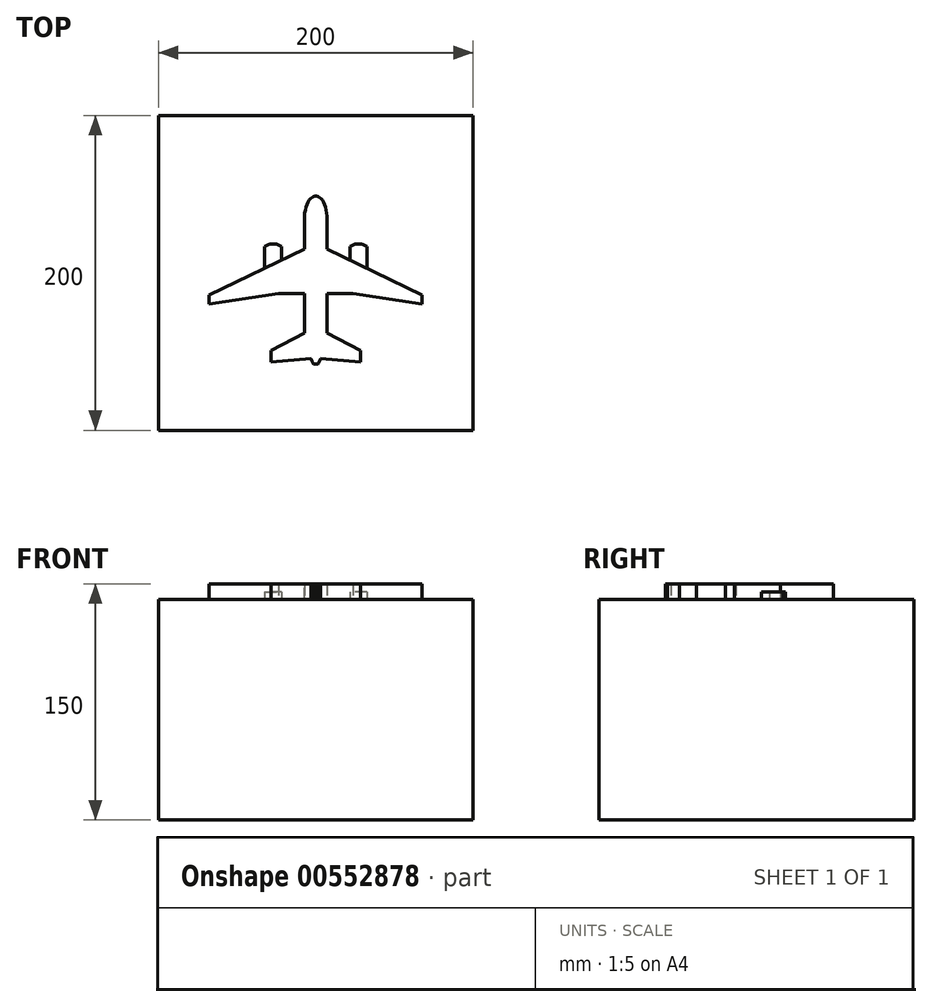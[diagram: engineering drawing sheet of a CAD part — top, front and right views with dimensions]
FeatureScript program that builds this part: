
annotation { "Feature Type Name" : "Feature", "Feature Type Description" : "" }
export const myFeature = defineFeature(function(context is Context, id is Id, definition is map)
    precondition{}
    {
        {
            var Q0;
            Q0=qCreatedBy(makeId("Top.planeOp"),FACE);
            var sketch = newSketch(context, id + "F0", { "sketchPlane" : qUnion([Q0])});
            skLineSegment(sketch, "E0.bottom", {"start": v(100, 100) * mm, "end": v(-100, 100) * mm});
            skLineSegment(sketch, "E0.top", {"start": v(100, -100) * mm, "end": v(-100, -100) * mm});
            skLineSegment(sketch, "E0.left", {"start": v(100, 100) * mm, "end": v(100, -100) * mm});
            skLineSegment(sketch, "E0.right", {"start": v(-100, 100) * mm, "end": v(-100, -100) * mm});
            skPoint(sketch, "E0.middle", {"position": v(0, 0) * mm});
            skLineSegment(sketch, "E1.left", {"start": v(7.25, 34.24) * mm, "end": v(7.25, -34.24) * mm});
            skLineSegment(sketch, "E1.right", {"start": v(-7.25, 34.24) * mm, "end": v(-7.25, -34.24) * mm});
            skEllipticalArc(sketch, "E2", {});
            skPoint(sketch, "E3.middle", {"position": v(0, -50.16) * mm});
            skPoint(sketch, "E4.middle", {"position": v(0, -55.01) * mm});
            skFitSpline(sketch, "E5", {"points": [v(-7.25, -34.24) * mm, v(-1.46, -57.87) * mm], "startDerivative": vector(0, -34.97) * mm, "endDerivative": vector(11.03, -22.41) * mm});
            skPoint(sketch, "E6", {"position": v(0, -57.83) * mm});
            skLineSegment(sketch, "E7", {"start": v(-1.46, -57.87) * mm, "end": v(0, -57.83) * mm});
            skLineSegment(sketch, "E8", {"start": v(0, -50.16) * mm, "end": v(0, -55.01) * mm});
            skFitSpline(sketch, "E9.MirrorCS", {"points": [v(7.25, -34.24) * mm, v(1.46, -57.87) * mm], "startDerivative": vector(0, -34.97) * mm, "endDerivative": vector(-11.03, -22.41) * mm});
            skLineSegment(sketch, "E10.MirrorCS", {"start": v(1.46, -57.87) * mm, "end": v(0, -57.83) * mm});
            skLineSegment(sketch, "E11", {"start": v(-7.25, 15.11) * mm, "end": v(-67.63, -14.05) * mm});
            skLineSegment(sketch, "E12", {"start": v(-67.63, -14.05) * mm, "end": v(-67.63, -19.77) * mm});
            skLineSegment(sketch, "E13", {"start": v(-67.63, -19.77) * mm, "end": v(-23.58, -13.1) * mm});
            skLineSegment(sketch, "E14", {"start": v(-23.58, -13.1) * mm, "end": v(-7.25, -13.1) * mm});
            skLineSegment(sketch, "E15.MirrorCS", {"start": v(23.58, -13.1) * mm, "end": v(7.25, -13.1) * mm});
            skLineSegment(sketch, "E16.MirrorCS", {"start": v(7.25, 15.11) * mm, "end": v(67.63, -14.05) * mm});
            skLineSegment(sketch, "E17.MirrorCS", {"start": v(67.63, -19.77) * mm, "end": v(23.58, -13.1) * mm});
            skLineSegment(sketch, "E18.MirrorCS", {"start": v(67.63, -14.05) * mm, "end": v(67.63, -19.77) * mm});
            skLineSegment(sketch, "E19", {"start": v(-7.15, -38.2) * mm, "end": v(-28.44, -49.13) * mm});
            skLineSegment(sketch, "E20", {"start": v(-28.44, -49.13) * mm, "end": v(-28.44, -56.5) * mm});
            skLineSegment(sketch, "E21", {"start": v(-28.44, -56.5) * mm, "end": v(-3.14, -54.39) * mm});
            skLineSegment(sketch, "E22.MirrorCS", {"start": v(7.15, -38.2) * mm, "end": v(28.44, -49.13) * mm});
            skLineSegment(sketch, "E23.MirrorCS", {"start": v(28.44, -49.13) * mm, "end": v(28.44, -56.5) * mm});
            skLineSegment(sketch, "E24.MirrorCS", {"start": v(28.44, -56.5) * mm, "end": v(3.14, -54.39) * mm});
            skLineSegment(sketch, "E25", {"start": v(-32.44, 2.94) * mm, "end": v(-32.44, 16.66) * mm});
            skLineSegment(sketch, "E26", {"start": v(-21.75, 16.61) * mm, "end": v(-21.8, 8.09) * mm});
            skArc(sketch, "E27", {"start": v(-21.75, 16.61) * mm, "mid": v(-27.09, 18.45) * mm, "end": v(-32.44, 16.66) * mm});
            skLineSegment(sketch, "E28.MirrorCS", {"start": v(21.75, 16.61) * mm, "end": v(21.8, 8.09) * mm});
            skArc(sketch, "E29.MirrorCS", {"start": v(21.75, 16.61) * mm, "mid": v(27.09, 18.45) * mm, "end": v(32.44, 16.66) * mm});
            skLineSegment(sketch, "E30.MirrorCS", {"start": v(32.44, 2.94) * mm, "end": v(32.44, 16.66) * mm});
            const initialGuessF0  = {"E2": [0, 0.034237012949378975, 0, 1, 0.014558184891939163, 0.007245441578226157, 4.71238898038469, 1.5707963267948966]};
            skSetInitialGuess(sketch, initialGuessF0);
            skSolve(sketch);
        }
        {
            var Q0;
            Q0=makeQuery(id+"F0.imprint","IMPRINT",FACE,{"disambiguationData":[TD([[makeQuery(id+"F0.imprint","IMPRINT",EDGE,{"derivedFrom":sQuery(id+"F0.wireOp",EDGE,"E0.bottom")}),1.0]])]});
            var Q1;
            {var subQ5=sQuery(id+"F0.wireOp",EDGE,"E12");Q1=makeQuery(id+"F0.imprint","IMPRINT",FACE,{"disambiguationData":[TD([[makeQuery(id+"F0.imprint","IMPRINT",EDGE,{"derivedFrom":subQ5}),1.0]])]});}
            var Q2;
            {var subQ0=sQuery(id+"F0.wireOp",EDGE,"E25");Q2=makeQuery(id+"F0.imprint","IMPRINT",FACE,{"disambiguationData":[TD([[makeQuery(id+"F0.imprint","IMPRINT",EDGE,{"derivedFrom":subQ0}),-1.0]])]});}
            var Q3;
            {var subQ0=sQuery(id+"F0.wireOp",EDGE,"E19");Q3=makeQuery(id+"F0.imprint","IMPRINT",FACE,{"disambiguationData":[TD([[makeQuery(id+"F0.imprint","IMPRINT",EDGE,{"derivedFrom":subQ0}),1.0]])]});}
            var Q4;
            {var subQ0=sQuery(id+"F0.wireOp",EDGE,"E22.MirrorCS");Q4=makeQuery(id+"F0.imprint","IMPRINT",FACE,{"disambiguationData":[TD([[makeQuery(id+"F0.imprint","IMPRINT",EDGE,{"derivedFrom":subQ0}),-1.0]])]});}
            var Q5;
            {var subQ0=sQuery(id+"F0.wireOp",EDGE,"E28.MirrorCS");Q5=makeQuery(id+"F0.imprint","IMPRINT",FACE,{"disambiguationData":[TD([[makeQuery(id+"F0.imprint","IMPRINT",EDGE,{"derivedFrom":subQ0}),1.0]])]});}
            extrude(context, id + "F1", {"entities" : qUnion([Q0, Q1, Q2, Q3, Q4, Q5]), "depth" : 140 * mm, "offsetDistance" : 25 * mm});
        }
        {
            var Q0;
            {var subQ6=sQuery(id+"F0.wireOp",EDGE,"E2");Q0=makeQuery(id+"F0.imprint","IMPRINT",FACE,{"disambiguationData":[TD([[makeQuery(id+"F0.imprint","IMPRINT",EDGE,{"derivedFrom":subQ6}),1.0]])]});}
            var Q1;
            {var subQ1=sQuery(id+"F0.wireOp",EDGE,"E15.MirrorCS");Q1=makeQuery(id+"F0.imprint","IMPRINT",FACE,{"disambiguationData":[TD([[makeQuery(id+"F0.imprint","IMPRINT",EDGE,{"derivedFrom":subQ1}),-1.0]])]});}
            extrude(context, id + "F2", {"entities" : qUnion([Q0, Q1]), "operationType" : NewBodyOperationType.ADD, "depth" : 140 * mm, "offsetDistance" : 25 * mm});
        }
        {
            var Q0;
            {var subQ0=sQuery(id+"F0.wireOp",EDGE,"E12");Q0=makeQuery(id+"F0.imprint","IMPRINT",FACE,{"disambiguationData":[TD([[makeQuery(id+"F0.imprint","IMPRINT",EDGE,{"derivedFrom":subQ0}),1.0]])]});}
            var Q1;
            {var subQ0=sQuery(id+"F0.wireOp",EDGE,"E25");Q1=makeQuery(id+"F0.imprint","IMPRINT",FACE,{"disambiguationData":[TD([[makeQuery(id+"F0.imprint","IMPRINT",EDGE,{"derivedFrom":subQ0}),-1.0]])]});}
            var Q2;
            {var subQ6=sQuery(id+"F0.wireOp",EDGE,"E2");Q2=makeQuery(id+"F0.imprint","IMPRINT",FACE,{"disambiguationData":[TD([[makeQuery(id+"F0.imprint","IMPRINT",EDGE,{"derivedFrom":subQ6}),1.0]])]});}
            var Q3;
            {var subQ1=sQuery(id+"F0.wireOp",EDGE,"E15.MirrorCS");Q3=makeQuery(id+"F0.imprint","IMPRINT",FACE,{"disambiguationData":[TD([[makeQuery(id+"F0.imprint","IMPRINT",EDGE,{"derivedFrom":subQ1}),-1.0]])]});}
            var Q4;
            {var subQ0=sQuery(id+"F0.wireOp",EDGE,"E28.MirrorCS");Q4=makeQuery(id+"F0.imprint","IMPRINT",FACE,{"disambiguationData":[TD([[makeQuery(id+"F0.imprint","IMPRINT",EDGE,{"derivedFrom":subQ0}),1.0]])]});}
            var Q5;
            {var subQ0=sQuery(id+"F0.wireOp",EDGE,"E22.MirrorCS");Q5=makeQuery(id+"F0.imprint","IMPRINT",FACE,{"disambiguationData":[TD([[makeQuery(id+"F0.imprint","IMPRINT",EDGE,{"derivedFrom":subQ0}),-1.0]])]});}
            var Q6;
            {var subQ0=sQuery(id+"F0.wireOp",EDGE,"E19");Q6=makeQuery(id+"F0.imprint","IMPRINT",FACE,{"disambiguationData":[TD([[makeQuery(id+"F0.imprint","IMPRINT",EDGE,{"derivedFrom":subQ0}),1.0]])]});}
            extrude(context, id + "F3", {"entities" : qUnion([Q0, Q1, Q2, Q3, Q4, Q5, Q6]), "operationType" : NewBodyOperationType.ADD, "depth" : 145 * mm, "offsetDistance" : 25 * mm});
        }
        {
            var Q0;
            {var subQ6=sQuery(id+"F0.wireOp",EDGE,"E2");Q0=makeQuery(id+"F0.imprint","IMPRINT",FACE,{"disambiguationData":[TD([[makeQuery(id+"F0.imprint","IMPRINT",EDGE,{"derivedFrom":subQ6}),1.0]])]});}
            var Q1;
            {var subQ1=sQuery(id+"F0.wireOp",EDGE,"E15.MirrorCS");Q1=makeQuery(id+"F0.imprint","IMPRINT",FACE,{"disambiguationData":[TD([[makeQuery(id+"F0.imprint","IMPRINT",EDGE,{"derivedFrom":subQ1}),-1.0]])]});}
            var Q2;
            {var subQ0=sQuery(id+"F0.wireOp",EDGE,"E12");Q2=makeQuery(id+"F0.imprint","IMPRINT",FACE,{"disambiguationData":[TD([[makeQuery(id+"F0.imprint","IMPRINT",EDGE,{"derivedFrom":subQ0}),1.0]])]});}
            var Q3;
            {var subQ0=sQuery(id+"F0.wireOp",EDGE,"E22.MirrorCS");Q3=makeQuery(id+"F0.imprint","IMPRINT",FACE,{"disambiguationData":[TD([[makeQuery(id+"F0.imprint","IMPRINT",EDGE,{"derivedFrom":subQ0}),-1.0]])]});}
            var Q4;
            {var subQ0=sQuery(id+"F0.wireOp",EDGE,"E19");Q4=makeQuery(id+"F0.imprint","IMPRINT",FACE,{"disambiguationData":[TD([[makeQuery(id+"F0.imprint","IMPRINT",EDGE,{"derivedFrom":subQ0}),1.0]])]});}
            extrude(context, id + "F4", {"entities" : qUnion([Q0, Q1, Q2, Q3, Q4]), "operationType" : NewBodyOperationType.ADD, "depth" : 150 * mm, "offsetDistance" : 25 * mm});
        }
        {
            var Q0;
            {var subQ6=sQuery(id+"F0.wireOp",EDGE,"E2");Q0=makeQuery(id+"F0.imprint","IMPRINT",FACE,{"disambiguationData":[TD([[makeQuery(id+"F0.imprint","IMPRINT",EDGE,{"derivedFrom":subQ6}),1.0]])]});}
            extrude(context, id + "F5", {"entities" : qUnion([Q0]), "operationType" : NewBodyOperationType.ADD, "depth" : 130 * mm, "offsetDistance" : 25 * mm});
        }
    });
